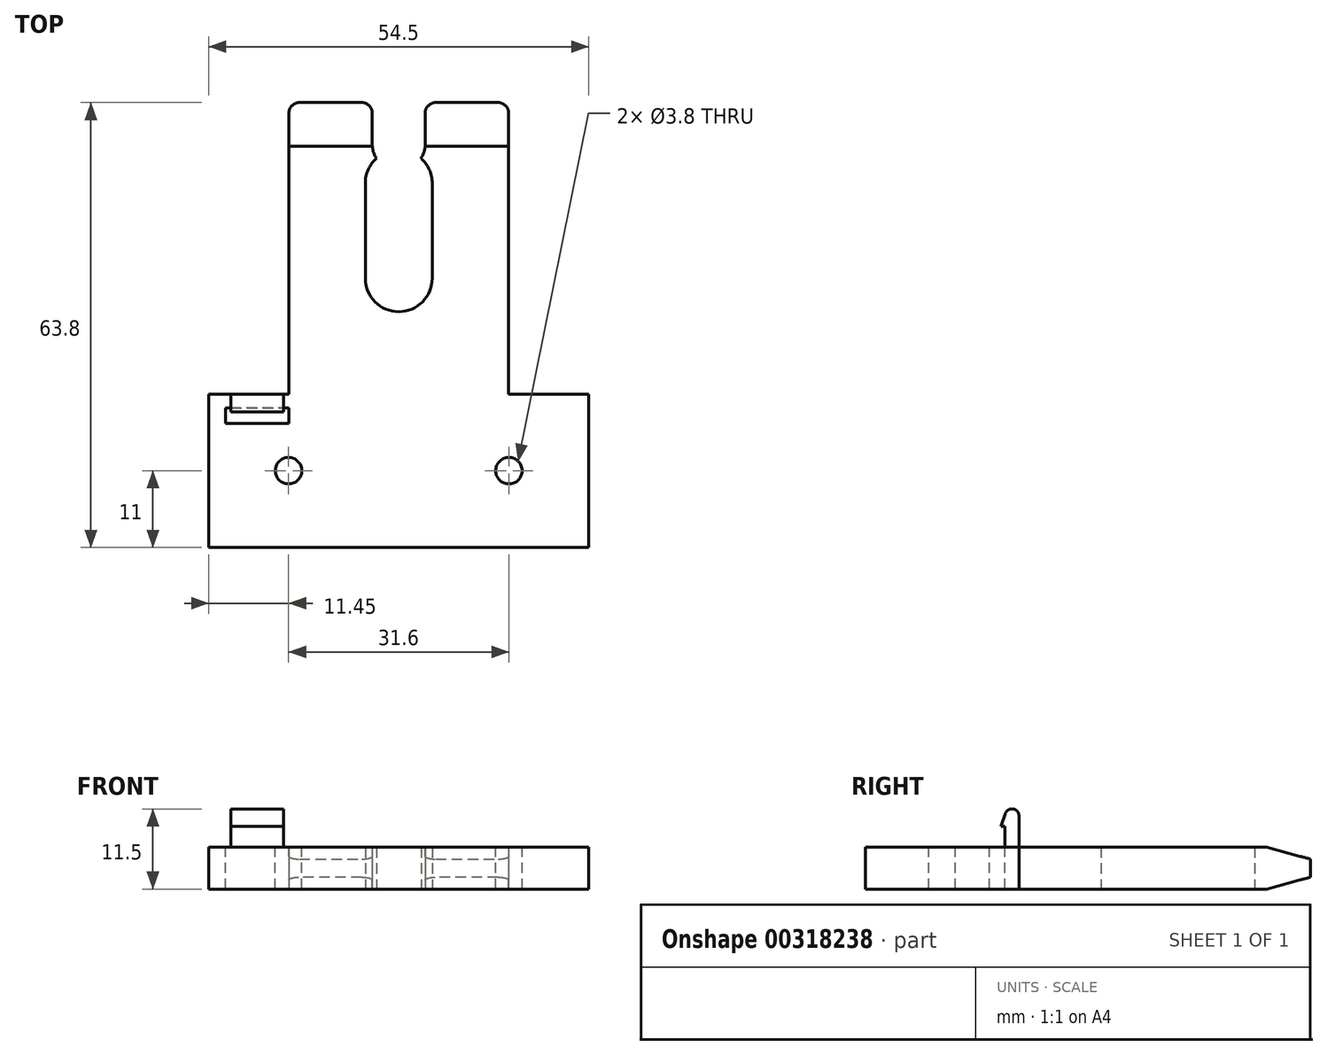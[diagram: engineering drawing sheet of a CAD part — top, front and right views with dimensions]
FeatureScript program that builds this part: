
annotation { "Feature Type Name" : "Feature", "Feature Type Description" : "" }
export const myFeature = defineFeature(function(context is Context, id is Id, definition is map)
    precondition{}
    {
        {
            var Q0;
            Q0=qCreatedBy(makeId("Top.planeOp"),FACE);
            var sketch = newSketch(context, id + "F0", { "sketchPlane" : qUnion([Q0])});
            skLineSegment(sketch, "E0.bottom", {"start": v(-14.25, 63.8) * mm, "end": v(-5.3, 63.8) * mm});
            skLineSegment(sketch, "E0.top", {"start": v(-27.25, 0) * mm, "end": v(27.25, 0) * mm});
            skLineSegment(sketch, "E0.left", {"start": v(-27.25, 22) * mm, "end": v(-27.25, 0) * mm});
            skLineSegment(sketch, "E0.right", {"start": v(27.25, 22) * mm, "end": v(27.25, 0) * mm});
            skLineSegment(sketch, "E1", {"start": v(0, 0) * mm, "end": v(0, 63.8) * mm, "construction": true});
            skLineSegment(sketch, "E2", {"start": v(-27.25, 22) * mm, "end": v(-15.75, 22) * mm});
            skLineSegment(sketch, "E3", {"start": v(-15.75, 22) * mm, "end": v(-15.75, 62.3) * mm});
            skLineSegment(sketch, "E4", {"start": v(-3.8, 62.3) * mm, "end": v(-3.8, 57.85) * mm});
            skArc(sketch, "E5", {"start": v(-4.8, 38.6) * mm, "mid": v(-3.4, 35.2) * mm, "end": v(0, 33.8) * mm});
            skLineSegment(sketch, "E6", {"start": v(-4.8, 38.6) * mm, "end": v(-4.8, 52.22) * mm});
            skArc(sketch, "E7", {"start": v(-3.2, 55.8) * mm, "mid": v(-4.38, 54.18) * mm, "end": v(-4.8, 52.22) * mm});
            skArc(sketch, "E8", {"start": v(-3.8, 57.85) * mm, "mid": v(-3.65, 56.78) * mm, "end": v(-3.2, 55.8) * mm});
            skLineSegment(sketch, "E9.MirrorCS", {"start": v(27.25, 22) * mm, "end": v(15.75, 22) * mm});
            skArc(sketch, "E10.MirrorCS", {"start": v(3.2, 55.8) * mm, "mid": v(4.38, 54.18) * mm, "end": v(4.8, 52.22) * mm});
            skLineSegment(sketch, "E11.MirrorCS", {"start": v(4.8, 38.6) * mm, "end": v(4.8, 52.22) * mm});
            skArc(sketch, "E12.MirrorCS", {"start": v(3.8, 57.85) * mm, "mid": v(3.65, 56.78) * mm, "end": v(3.2, 55.8) * mm});
            skArc(sketch, "E13.MirrorCS", {"start": v(4.8, 38.6) * mm, "mid": v(3.4, 35.2) * mm, "end": v(0, 33.8) * mm});
            skLineSegment(sketch, "E14.MirrorCS", {"start": v(3.8, 62.3) * mm, "end": v(3.8, 57.85) * mm});
            skLineSegment(sketch, "E15.MirrorCS", {"start": v(15.75, 22) * mm, "end": v(15.75, 62.3) * mm});
            skLineSegment(sketch, "E16.trimOffspring", {"start": v(5.3, 63.8) * mm, "end": v(14.25, 63.8) * mm});
            skPoint(sketch, "E17.visualSharp", {"position": v(-15.75, 63.8) * mm});
            skArc(sketch, "E17.filletArc", {"start": v(-14.25, 63.8) * mm, "mid": v(-15.31, 63.36) * mm, "end": v(-15.75, 62.3) * mm});
            skPoint(sketch, "E18.visualSharp", {"position": v(-3.8, 63.8) * mm});
            skArc(sketch, "E18.filletArc", {"start": v(-3.8, 62.3) * mm, "mid": v(-4.24, 63.36) * mm, "end": v(-5.3, 63.8) * mm});
            skPoint(sketch, "E19.visualSharp", {"position": v(3.8, 63.8) * mm});
            skArc(sketch, "E19.filletArc", {"start": v(5.3, 63.8) * mm, "mid": v(4.24, 63.36) * mm, "end": v(3.8, 62.3) * mm});
            skPoint(sketch, "E20.visualSharp", {"position": v(15.75, 63.8) * mm});
            skArc(sketch, "E20.filletArc", {"start": v(15.75, 62.3) * mm, "mid": v(15.31, 63.36) * mm, "end": v(14.25, 63.8) * mm});
            skSolve(sketch);
        }
        {
            var Q0;
            Q0 = qSketchRegion(id + "F0", true);
            extrude(context, id + "F1", {"entities" : qUnion([Q0]), "depth" : 6 * mm});
        }
        {
            var Q0;
            Q0=makeQuery(id+"F1.opExtrude","CAP_EDGE",EDGE,{"disambiguationData":[OSD([sQuery(id+"F0.wireOp",EDGE,"E16.trimOffspring")])],"isStart":false});
            var Q1;
            Q1=makeQuery(id+"F1.opExtrude","CAP_EDGE",EDGE,{"disambiguationData":[OSD([sQuery(id+"F0.wireOp",EDGE,"E0.bottom")])],"isStart":false});
            chamfer(context, id + "F2", {"entities" : qUnion([Q0, Q1]), "chamferType" : ChamferType.TWO_OFFSETS, "width1" : 1.7 * mm, "oppositeDirection" : false, "width2" : 6.3 * mm});
        }
        {
            var Q0;
            Q0=makeQuery(id+"F1.opExtrude","CAP_EDGE",EDGE,{"disambiguationData":[OSD([sQuery(id+"F0.wireOp",EDGE,"E16.trimOffspring")])],"isStart":true});
            var Q1;
            Q1=makeQuery(id+"F1.opExtrude","CAP_EDGE",EDGE,{"disambiguationData":[OSD([sQuery(id+"F0.wireOp",EDGE,"E0.bottom")])],"isStart":true});
            chamfer(context, id + "F3", {"entities" : qUnion([Q0, Q1]), "chamferType" : ChamferType.TWO_OFFSETS, "width1" : 6.3 * mm, "oppositeDirection" : false, "width2" : 1.7 * mm});
        }
        {
            var Q0;
            Q0=makeQuery(id+"F1.opExtrude","CAP_FACE",FACE,{"disambiguationData":[OSD([sQuery(id+"F0.wireOp",EDGE,"E0.bottom"),sQuery(id+"F0.wireOp",EDGE,"E0.top"),sQuery(id+"F0.wireOp",EDGE,"E0.left"),sQuery(id+"F0.wireOp",EDGE,"E0.right"),sQuery(id+"F0.wireOp",EDGE,"E2"),sQuery(id+"F0.wireOp",EDGE,"E3"),sQuery(id+"F0.wireOp",EDGE,"E4"),sQuery(id+"F0.wireOp",EDGE,"E5"),sQuery(id+"F0.wireOp",EDGE,"E6"),sQuery(id+"F0.wireOp",EDGE,"E7"),sQuery(id+"F0.wireOp",EDGE,"E8"),sQuery(id+"F0.wireOp",EDGE,"E9.MirrorCS"),sQuery(id+"F0.wireOp",EDGE,"E10.MirrorCS"),sQuery(id+"F0.wireOp",EDGE,"E11.MirrorCS"),sQuery(id+"F0.wireOp",EDGE,"E12.MirrorCS"),sQuery(id+"F0.wireOp",EDGE,"E13.MirrorCS"),sQuery(id+"F0.wireOp",EDGE,"E14.MirrorCS"),sQuery(id+"F0.wireOp",EDGE,"E15.MirrorCS"),sQuery(id+"F0.wireOp",EDGE,"E16.trimOffspring")])],"isStart":false});
            var sketch = newSketch(context, id + "F4", { "sketchPlane" : qUnion([Q0])});
            skLineSegment(sketch, "E21.bottom", {"start": v(-15.75, 20) * mm, "end": v(-24.85, 20) * mm});
            skLineSegment(sketch, "E21.top", {"start": v(-15.75, 17.8) * mm, "end": v(-24.85, 17.8) * mm});
            skLineSegment(sketch, "E21.left", {"start": v(-15.75, 20) * mm, "end": v(-15.75, 17.8) * mm});
            skLineSegment(sketch, "E21.right", {"start": v(-24.85, 20) * mm, "end": v(-24.85, 17.8) * mm});
            skSolve(sketch);
        }
        {
            var Q0;
            Q0 = qSketchRegion(id + "F4", true);
            extrude(context, id + "F5", {"entities" : qUnion([Q0]), "operationType" : NewBodyOperationType.REMOVE, "endBound" : BoundingType.THROUGH_ALL, "oppositeDirection" : true, "depth" : 25 * mm});
        }
        {
            var Q0;
            Q0=makeQuery(id+"F5.boolean.opBoolean","COPY",FACE,{"derivedFrom":makeQuery(id+"F5.opExtrude","SWEPT_FACE",FACE,{"disambiguationData":[OSD([sQuery(id+"F4.wireOp",EDGE,"E21.left")])]})});
            var Q1;
            Q1=makeQuery(id+"F5.boolean.opBoolean","COPY",FACE,{"derivedFrom":makeQuery(id+"F5.opExtrude","SWEPT_FACE",FACE,{"disambiguationData":[OSD([sQuery(id+"F4.wireOp",EDGE,"E21.right")])]})});
            cPlane(context, id + "F6", {"entities" : qUnion([Q0, Q1]), "cplaneType" : CPlaneType.MID_PLANE, "offset" : 25 * mm, "width" : 150 * mm, "height" : 150 * mm});
        }
        {
            var Q0;
            Q0=qCreatedBy(id+"F6.planeOp",FACE);
            var sketch = newSketch(context, id + "F7", { "sketchPlane" : qUnion([Q0])});
            skLineSegment(sketch, "E22", {"start": v(-22, 6) * mm, "end": v(-22, 10.5) * mm});
            skLineSegment(sketch, "E23", {"start": v(-22, 6) * mm, "end": v(-20, 6) * mm});
            skLineSegment(sketch, "E24", {"start": v(-20, 6) * mm, "end": v(-20, 9) * mm});
            skLineSegment(sketch, "E25", {"start": v(-20, 9) * mm, "end": v(-19.4, 9) * mm});
            skArc(sketch, "E26", {"start": v(-20.06, 10.84) * mm, "mid": v(-21.17, 11.49) * mm, "end": v(-22, 10.5) * mm});
            skPoint(sketch, "E26.second.point", {"position": v(-20, 10.5) * mm});
            skPoint(sketch, "E26.third.point", {"position": v(-21, 11.5) * mm});
            skLineSegment(sketch, "E27", {"start": v(-19.4, 9) * mm, "end": v(-20.06, 10.84) * mm});
            skSolve(sketch);
        }
        {
            var Q0;
            Q0 = qSketchRegion(id + "F7", true);
            extrude(context, id + "F8", {"entities" : qUnion([Q0]), "operationType" : NewBodyOperationType.ADD, "endBound" : BoundingType.SYMMETRIC, "depth" : 7.5 * mm, "hasSecondDirection" : true, "secondDirectionOppositeDirection" : false, "secondDirectionDepth" : 1.5 * mm});
        }
        {
            var Q0;
            Q0=makeQuery(id+"F1.opExtrude","SWEPT_FACE",FACE,{"disambiguationData":[OSD([sQuery(id+"F0.wireOp",EDGE,"E0.top")])]});
            var Q1;
            Q1=makeQuery(id+"F8.boolean.opBoolean","MERGE",FACE,{"derivedFrom":[makeQuery(id+"F1.opExtrude","SWEPT_FACE",FACE,{"disambiguationData":[OSD([sQuery(id+"F0.wireOp",EDGE,"E2")])]}),makeQuery(id+"F8.opExtrude","SWEPT_FACE",FACE,{"disambiguationData":[OSD([sQuery(id+"F7.wireOp",EDGE,"E22")])]})]});
            cPlane(context, id + "F9", {"entities" : qUnion([Q0, Q1]), "cplaneType" : CPlaneType.MID_PLANE, "offset" : 0 * mm, "width" : 150 * mm, "height" : 150 * mm});
        }
        {
            var Q0;
            Q0=makeQuery(id+"F1.opExtrude","CAP_FACE",FACE,{"disambiguationData":[OSD([sQuery(id+"F0.wireOp",EDGE,"E0.bottom"),sQuery(id+"F0.wireOp",EDGE,"E0.top"),sQuery(id+"F0.wireOp",EDGE,"E0.left"),sQuery(id+"F0.wireOp",EDGE,"E0.right"),sQuery(id+"F0.wireOp",EDGE,"E2"),sQuery(id+"F0.wireOp",EDGE,"E3"),sQuery(id+"F0.wireOp",EDGE,"E4"),sQuery(id+"F0.wireOp",EDGE,"E5"),sQuery(id+"F0.wireOp",EDGE,"E6"),sQuery(id+"F0.wireOp",EDGE,"E7"),sQuery(id+"F0.wireOp",EDGE,"E8"),sQuery(id+"F0.wireOp",EDGE,"E9.MirrorCS"),sQuery(id+"F0.wireOp",EDGE,"E10.MirrorCS"),sQuery(id+"F0.wireOp",EDGE,"E11.MirrorCS"),sQuery(id+"F0.wireOp",EDGE,"E12.MirrorCS"),sQuery(id+"F0.wireOp",EDGE,"E13.MirrorCS"),sQuery(id+"F0.wireOp",EDGE,"E14.MirrorCS"),sQuery(id+"F0.wireOp",EDGE,"E15.MirrorCS"),sQuery(id+"F0.wireOp",EDGE,"E16.trimOffspring")])],"isStart":false});
            var sketch = newSketch(context, id + "F10", { "sketchPlane" : qUnion([Q0])});
            skCircle(sketch, "E28", {"center": v(-15.8, 11) * mm, "radius": 1.9 * mm});
            skPoint(sketch, "E28.centerSnap0", {"position": v(-27.25, 11) * mm});
            skCircle(sketch, "E29.MirrorC", {"center": v(15.8, 11) * mm, "radius": 1.9 * mm});
            skSolve(sketch);
        }
        {
            var Q0;
            Q0 = qSketchRegion(id + "F10", true);
            extrude(context, id + "F11", {"entities" : qUnion([Q0]), "operationType" : NewBodyOperationType.REMOVE, "endBound" : BoundingType.THROUGH_ALL, "oppositeDirection" : true, "depth" : 25 * mm});
        }
    });
